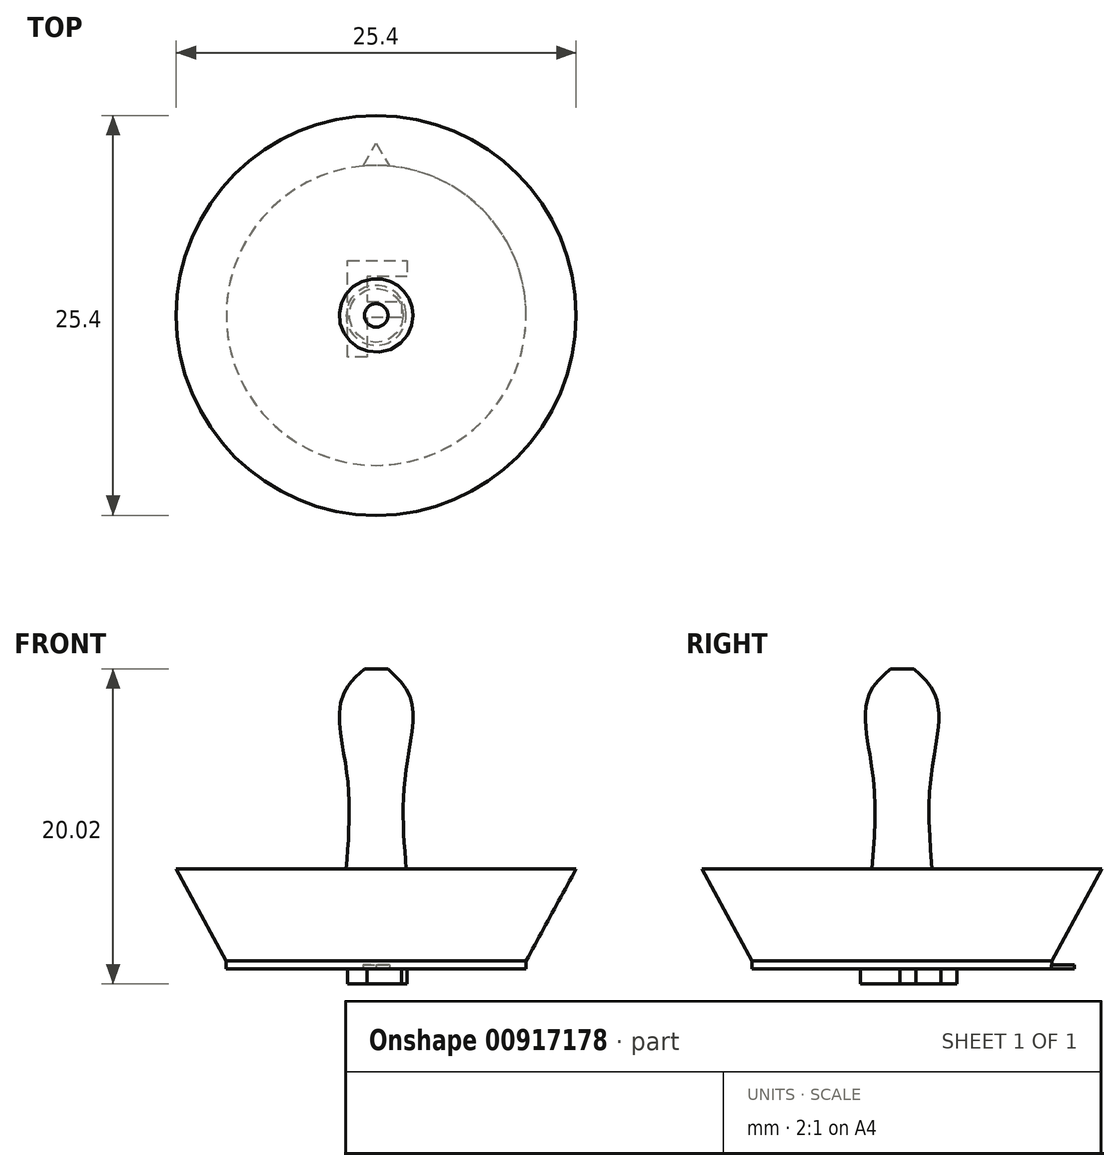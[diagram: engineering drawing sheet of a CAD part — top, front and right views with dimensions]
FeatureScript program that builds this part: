
annotation { "Feature Type Name" : "Feature", "Feature Type Description" : "" }
export const myFeature = defineFeature(function(context is Context, id is Id, definition is map)
    precondition{}
    {
        {
            var Q0;
            Q0=qCreatedBy(makeId("Top.planeOp"),FACE);
            var sketch = newSketch(context, id + "F0", { "sketchPlane" : qUnion([Q0])});
            skCircle(sketch, "E0", {"center": v(0, 0) * mm, "radius": 9.53 * mm});
            skSolve(sketch);
        }
        {
            var Q0;
            Q0=qCreatedBy(makeId("Top.planeOp"),FACE);
            cPlane(context, id + "F1", {"entities" : qUnion([Q0]), "cplaneType" : CPlaneType.OFFSET, "offset" : 6.35 * mm, "width" : 152.4 * mm, "height" : 152.4 * mm});
        }
        {
            var Q0;
            Q0=qCreatedBy(id+"F1.planeOp",FACE);
            var sketch = newSketch(context, id + "F2", { "sketchPlane" : qUnion([Q0])});
            skCircle(sketch, "E1", {"center": v(0, 0) * mm, "radius": 12.7 * mm});
            skSolve(sketch);
        }
        {
            var Q0;
            Q0=qCreatedBy(makeId("Top.planeOp"),FACE);
            var sketch = newSketch(context, id + "F3", { "sketchPlane" : qUnion([Q0])});
            skCircle(sketch, "E2.cCircle", {"center": v(0, 9.97) * mm, "radius": 0.48 * mm, "construction": true});
            skLineSegment(sketch, "E2.0", {"start": v(0.84, 9.49) * mm, "end": v(-0.84, 9.49) * mm});
            skLineSegment(sketch, "E2.1", {"start": v(-0.84, 9.49) * mm, "end": v(0, 10.94) * mm});
            skLineSegment(sketch, "E2.2", {"start": v(0, 10.94) * mm, "end": v(0.84, 9.49) * mm});
            skPoint(sketch, "E2.0.midPoint", {"position": v(0, 9.49) * mm});
            skSolve(sketch);
        }
        {
            var Q0;
            Q0 = qSketchRegion(id + "F0", true);
            extrude(context, id + "F4", {"entities" : qUnion([Q0]), "depth" : 0.5 * mm, "offsetDistance" : 25.4 * mm});
        }
        {
            var Q0;
            Q0 = qSketchRegion(id + "F3", true);
            extrude(context, id + "F5", {"entities" : qUnion([Q0]), "operationType" : NewBodyOperationType.ADD, "depth" : 0.25 * mm, "offsetDistance" : 25.4 * mm});
        }
        {
            var Q1;
            Q1=makeQuery(id+"F2.imprint","IMPRINT",FACE,{"disambiguationData":[TD([[makeQuery(id+"F2.imprint","IMPRINT",EDGE,{"derivedFrom":sQuery(id+"F2.wireOp",EDGE,"E1")}),1.0]])]});
            var Q2;
            Q2=makeQuery(id+"F4.opExtrude","CAP_FACE",FACE,{"disambiguationData":[OSD([sQuery(id+"F0.wireOp",EDGE,"E0")])],"isStart":false});
            loft(context, id + "F6", {"operationType" : NewBodyOperationType.ADD, "sheetProfilesArray" : [{ "sheetProfileEntities" : qUnion([Q1]) }, { "sheetProfileEntities" : qUnion([Q2]) }]});
        }
        {
            var Q0;
            Q0=qCreatedBy(id+"F1.planeOp",FACE);
            cPlane(context, id + "F7", {"entities" : qUnion([Q0]), "cplaneType" : CPlaneType.OFFSET, "offset" : 6.35 * mm, "width" : 152.4 * mm, "height" : 152.4 * mm});
        }
        {
            var Q0;
            Q0=qCreatedBy(id+"F1.planeOp",FACE);
            var sketch = newSketch(context, id + "F8", { "sketchPlane" : qUnion([Q0])});
            skCircle(sketch, "E3", {"center": v(0, 0) * mm, "radius": 1.9 * mm});
            skSolve(sketch);
        }
        {
            var Q0;
            Q0=qCreatedBy(id+"F7.planeOp",FACE);
            var sketch = newSketch(context, id + "F9", { "sketchPlane" : qUnion([Q0])});
            skCircle(sketch, "E4", {"center": v(0, 0) * mm, "radius": 1.9 * mm});
            skCircle(sketch, "E5", {"center": v(-29.82, 0) * mm, "radius": 1.26 * mm});
            skCircle(sketch, "E6", {"center": v(8.42, 0) * mm, "radius": 1.25 * mm});
            skSolve(sketch);
        }
        {
            var Q0;
            Q0=qCreatedBy(id+"F7.planeOp",FACE);
            cPlane(context, id + "F10", {"entities" : qUnion([Q0]), "cplaneType" : CPlaneType.OFFSET, "offset" : 5.08 * mm, "width" : 152.4 * mm, "height" : 152.4 * mm});
        }
        {
            var Q0;
            Q0=qCreatedBy(id+"F10.planeOp",FACE);
            var sketch = newSketch(context, id + "F11", { "sketchPlane" : qUnion([Q0])});
            skCircle(sketch, "E7", {"center": v(0, 0) * mm, "radius": 1.9 * mm});
            skSolve(sketch);
        }
        {
            var Q0;
            Q0=qCreatedBy(id+"F10.planeOp",FACE);
            cPlane(context, id + "F12", {"entities" : qUnion([Q0]), "cplaneType" : CPlaneType.OFFSET, "offset" : 1.27 * mm, "width" : 152.4 * mm, "height" : 152.4 * mm});
        }
        {
            var Q0;
            Q0=qCreatedBy(id+"F12.planeOp",FACE);
            var sketch = newSketch(context, id + "F13", { "sketchPlane" : qUnion([Q0])});
            skCircle(sketch, "E8", {"center": v(0, 0) * mm, "radius": 0.75 * mm});
            skSolve(sketch);
        }
        {
            var Q1;
            Q1=makeQuery(id+"F13.imprint","IMPRINT",FACE,{"disambiguationData":[TD([[makeQuery(id+"F13.imprint","IMPRINT",EDGE,{"derivedFrom":sQuery(id+"F13.wireOp",EDGE,"E8")}),1.0]])]});
            var Q2;
            Q2=makeQuery(id+"F11.imprint","IMPRINT",FACE,{"disambiguationData":[TD([[makeQuery(id+"F11.imprint","IMPRINT",EDGE,{"derivedFrom":sQuery(id+"F11.wireOp",EDGE,"E7")}),1.0]])]});
            var Q3;
            Q3=makeQuery(id+"F9.imprint","IMPRINT",FACE,{"disambiguationData":[TD([[makeQuery(id+"F9.imprint","IMPRINT",EDGE,{"derivedFrom":sQuery(id+"F9.wireOp",EDGE,"E4")}),1.0]])]});
            var Q4;
            Q4=makeQuery(id+"F8.imprint","IMPRINT",FACE,{"disambiguationData":[TD([[makeQuery(id+"F8.imprint","IMPRINT",EDGE,{"derivedFrom":sQuery(id+"F8.wireOp",EDGE,"E3")}),1.0]])]});
            loft(context, id + "F14", {"operationType" : NewBodyOperationType.ADD, "sheetProfilesArray" : [{ "sheetProfileEntities" : qUnion([Q1]) }, { "sheetProfileEntities" : qUnion([Q2]) }, { "sheetProfileEntities" : qUnion([Q3]) }, { "sheetProfileEntities" : qUnion([Q4]) }]});
        }
        {
            var Q0;
            Q0=makeQuery(id+"F0.imprint","IMPRINT",FACE,{"disambiguationData":[TD([[makeQuery(id+"F0.imprint","IMPRINT",EDGE,{"derivedFrom":sQuery(id+"F0.wireOp",EDGE,"E0")}),1.0]])]});
            var sketch = newSketch(context, id + "F15", { "sketchPlane" : qUnion([Q0])});
            skText(sketch, "E9", { "text": "F", "fontName": "NotoSansCJKjp-Bold.otf"});
            const initialGuessF15  = {"E9": [-0.00256, -0.00263, 1, 0, 0.00596]};
            skSetInitialGuess(sketch, initialGuessF15);
            skSolve(sketch);
        }
        {
            var Q0;
            Q0 = qSketchRegion(id + "F15", true);
            extrude(context, id + "F16", {"entities" : qUnion([Q0]), "operationType" : NewBodyOperationType.ADD, "depth" : 2.74 * mm, "offsetDistance" : 25.4 * mm, "hasSecondDirection" : true, "secondDirectionOppositeDirection" : true, "secondDirectionDepth" : 0.97 * mm});
        }
    });
